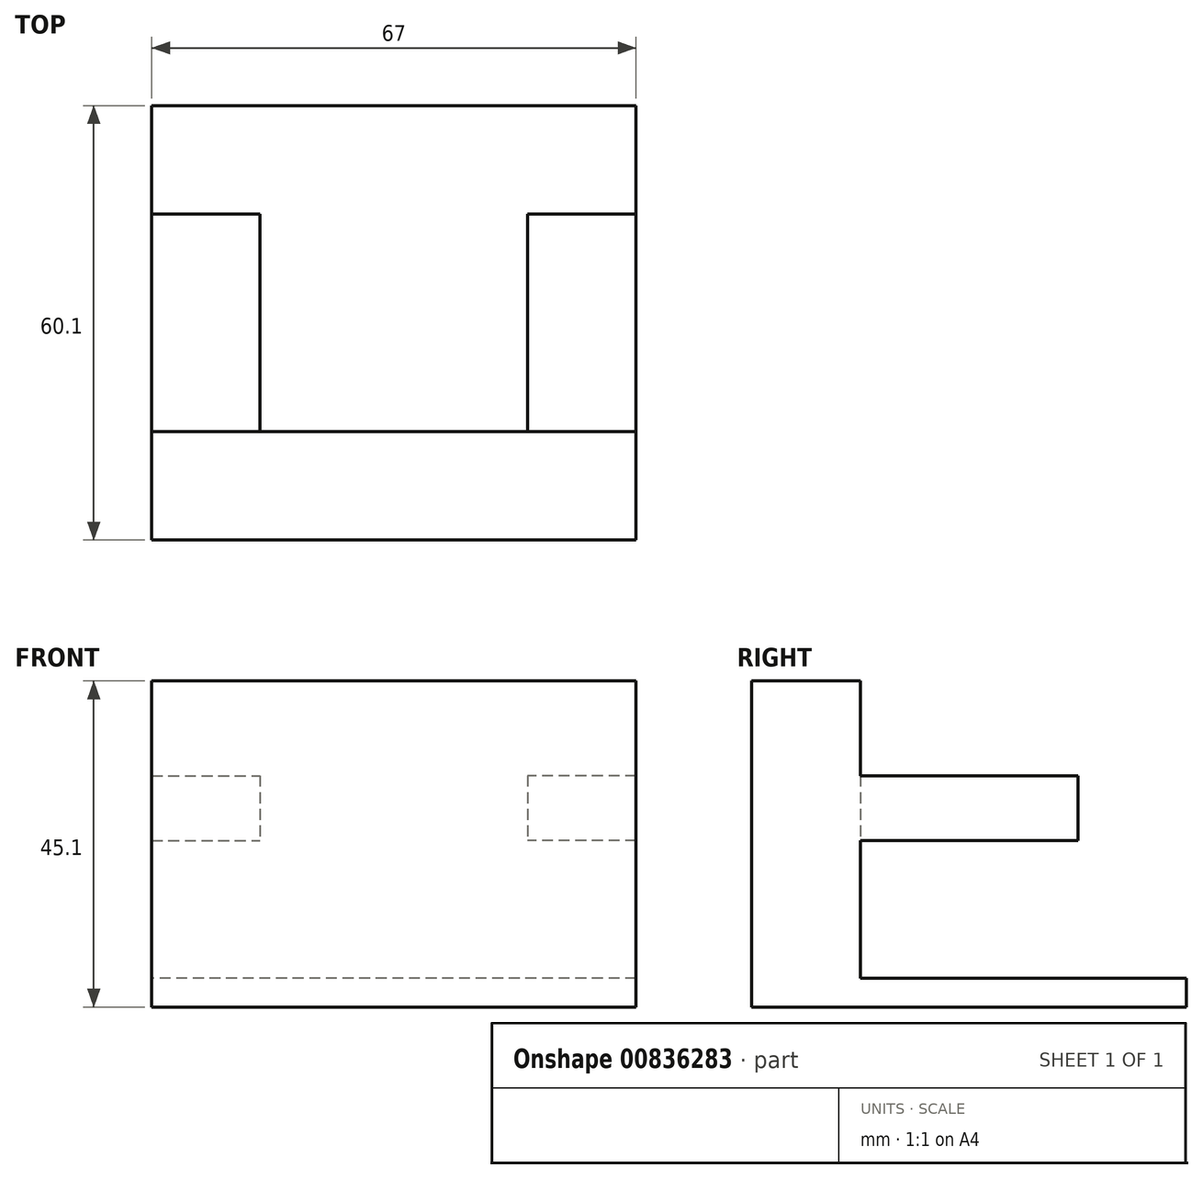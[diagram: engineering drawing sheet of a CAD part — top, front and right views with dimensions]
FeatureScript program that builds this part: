
annotation { "Feature Type Name" : "Feature", "Feature Type Description" : "" }
export const myFeature = defineFeature(function(context is Context, id is Id, definition is map)
    precondition{}
    {
        {
            var Q0;
            Q0=qCreatedBy(makeId("Top.planeOp"),FACE);
            var sketch = newSketch(context, id + "F0", { "sketchPlane" : qUnion([Q0])});
            skLineSegment(sketch, "E0.bottom", {"start": v(33.5, 30.05) * mm, "end": v(-33.5, 30.05) * mm});
            skLineSegment(sketch, "E0.top", {"start": v(33.5, -30.05) * mm, "end": v(-33.5, -30.05) * mm});
            skLineSegment(sketch, "E0.left", {"start": v(33.5, 30.05) * mm, "end": v(33.5, -30.05) * mm});
            skLineSegment(sketch, "E0.right", {"start": v(-33.5, 30.05) * mm, "end": v(-33.5, -30.05) * mm});
            skPoint(sketch, "E0.middle", {"position": v(0, 0) * mm});
            skLineSegment(sketch, "E1.bottom", {"start": v(18.5, 15.05) * mm, "end": v(-18.5, 15.05) * mm});
            skLineSegment(sketch, "E1.top", {"start": v(18.5, -15.05) * mm, "end": v(-18.5, -15.05) * mm});
            skLineSegment(sketch, "E1.left", {"start": v(18.5, 15.05) * mm, "end": v(18.5, -15.05) * mm});
            skLineSegment(sketch, "E1.right", {"start": v(-18.5, 15.05) * mm, "end": v(-18.5, -15.05) * mm});
            skLineSegment(sketch, "E2", {"start": v(-18.5, -15.05) * mm, "end": v(-18.5, -30.05) * mm});
            skLineSegment(sketch, "E3", {"start": v(18.5, -15.05) * mm, "end": v(18.5, -30.05) * mm});
            skLineSegment(sketch, "E4", {"start": v(-18.5, -15.05) * mm, "end": v(-33.5, -15.05) * mm});
            skLineSegment(sketch, "E5", {"start": v(18.5, -15.05) * mm, "end": v(33.5, -15.05) * mm});
            skSolve(sketch);
        }
        {
            var Q0;
            Q0=makeQuery(id+"F0.imprint","IMPRINT",FACE,{"disambiguationData":[TD([[makeQuery(id+"F0.imprint","IMPRINT",EDGE,{"derivedFrom":sQuery(id+"F0.wireOp",EDGE,"E0.bottom")}),1.0]])]});
            var Q1;
            Q1=makeQuery(id+"F0.imprint","IMPRINT",FACE,{"disambiguationData":[TD([[makeQuery(id+"F0.imprint","IMPRINT",EDGE,{"derivedFrom":sQuery(id+"F0.wireOp",EDGE,"E1.bottom")}),1.0]])]});
            var Q2;
            Q2=makeQuery(id+"F0.imprint","IMPRINT",FACE,{"disambiguationData":[TD([[makeQuery(id+"F0.imprint","IMPRINT",EDGE,{"derivedFrom":sQuery(id+"F0.wireOp",EDGE,"E1.top")}),1.0]])]});
            var Q3;
            {var subQ3=sQuery(id+"F0.wireOp",EDGE,"E2");Q3=makeQuery(id+"F0.imprint","IMPRINT",FACE,{"disambiguationData":[TD([[makeQuery(id+"F0.imprint","IMPRINT",EDGE,{"derivedFrom":subQ3}),-1.0]])]});}
            var Q4;
            {var subQ3=sQuery(id+"F0.wireOp",EDGE,"E3");Q4=makeQuery(id+"F0.imprint","IMPRINT",FACE,{"disambiguationData":[TD([[makeQuery(id+"F0.imprint","IMPRINT",EDGE,{"derivedFrom":subQ3}),1.0]])]});}
            extrude(context, id + "F1", {"entities" : qUnion([Q0, Q1, Q2, Q3, Q4]), "oppositeDirection" : true, "depth" : 4 * mm, "offsetDistance" : 25 * mm});
        }
        {
            var Q0;
            Q0=makeQuery(id+"F0.imprint","IMPRINT",FACE,{"disambiguationData":[TD([[makeQuery(id+"F0.imprint","IMPRINT",EDGE,{"derivedFrom":sQuery(id+"F0.wireOp",EDGE,"E1.top")}),1.0]])]});
            var Q1;
            {var subQ3=sQuery(id+"F0.wireOp",EDGE,"E2");Q1=makeQuery(id+"F0.imprint","IMPRINT",FACE,{"disambiguationData":[TD([[makeQuery(id+"F0.imprint","IMPRINT",EDGE,{"derivedFrom":subQ3}),-1.0]])]});}
            var Q2;
            {var subQ3=sQuery(id+"F0.wireOp",EDGE,"E3");Q2=makeQuery(id+"F0.imprint","IMPRINT",FACE,{"disambiguationData":[TD([[makeQuery(id+"F0.imprint","IMPRINT",EDGE,{"derivedFrom":subQ3}),1.0]])]});}
            extrude(context, id + "F2", {"entities" : qUnion([Q0, Q1, Q2]), "operationType" : NewBodyOperationType.ADD, "depth" : 41.1 * mm, "offsetDistance" : 25 * mm});
        }
        {
            var Q0;
            Q0=makeQuery(id+"F2.opExtrude","SWEPT_FACE",FACE,{"disambiguationData":[OSD([sQuery(id+"F0.wireOp",EDGE,"E1.top"),sQuery(id+"F0.wireOp",EDGE,"E4"),sQuery(id+"F0.wireOp",EDGE,"E5")])]});
            var sketch = newSketch(context, id + "F3", { "sketchPlane" : qUnion([Q0])});
            skLineSegment(sketch, "E6", {"start": v(33.5, 41.1) * mm, "end": v(18.5, 41.1) * mm});
            skLineSegment(sketch, "E7", {"start": v(-33.5, 41.1) * mm, "end": v(-18.5, 41.1) * mm});
            skLineSegment(sketch, "E8", {"start": v(18.5, 41.1) * mm, "end": v(18.5, 0) * mm});
            skLineSegment(sketch, "E9", {"start": v(-18.5, 41.1) * mm, "end": v(-18.5, 0) * mm});
            skLineSegment(sketch, "E10", {"start": v(33.5, 19) * mm, "end": v(18.5, 19) * mm});
            skLineSegment(sketch, "E11", {"start": v(33.5, 19) * mm, "end": v(33.5, 0) * mm});
            skLineSegment(sketch, "E12", {"start": v(33.5, 28) * mm, "end": v(18.5, 28) * mm});
            skLineSegment(sketch, "E13", {"start": v(33.5, 28) * mm, "end": v(33.5, 19) * mm});
            skLineSegment(sketch, "E14", {"start": v(-33.5, 0) * mm, "end": v(-33.5, 19) * mm});
            skLineSegment(sketch, "E15", {"start": v(-33.5, 19) * mm, "end": v(-18.5, 19) * mm});
            skLineSegment(sketch, "E16", {"start": v(-33.5, 19) * mm, "end": v(-33.5, 28) * mm});
            skLineSegment(sketch, "E17", {"start": v(-33.5, 28) * mm, "end": v(-18.5, 28) * mm});
            skSolve(sketch);
        }
        {
            var Q0;
            {var subQ0=sQuery(id+"F3.wireOp",EDGE,"E10");Q0=makeQuery(id+"F3.imprint","IMPRINT",FACE,{"disambiguationData":[TD([[makeQuery(id+"F3.imprint","IMPRINT",EDGE,{"derivedFrom":subQ0}),-1.0]])]});}
            var Q1;
            {var subQ0=sQuery(id+"F3.wireOp",EDGE,"E15");Q1=makeQuery(id+"F3.imprint","IMPRINT",FACE,{"disambiguationData":[TD([[makeQuery(id+"F3.imprint","IMPRINT",EDGE,{"derivedFrom":subQ0}),1.0]])]});}
            extrude(context, id + "F4", {"entities" : qUnion([Q0, Q1]), "operationType" : NewBodyOperationType.ADD, "depth" : 30.1 * mm, "offsetDistance" : 25 * mm});
        }
    });
